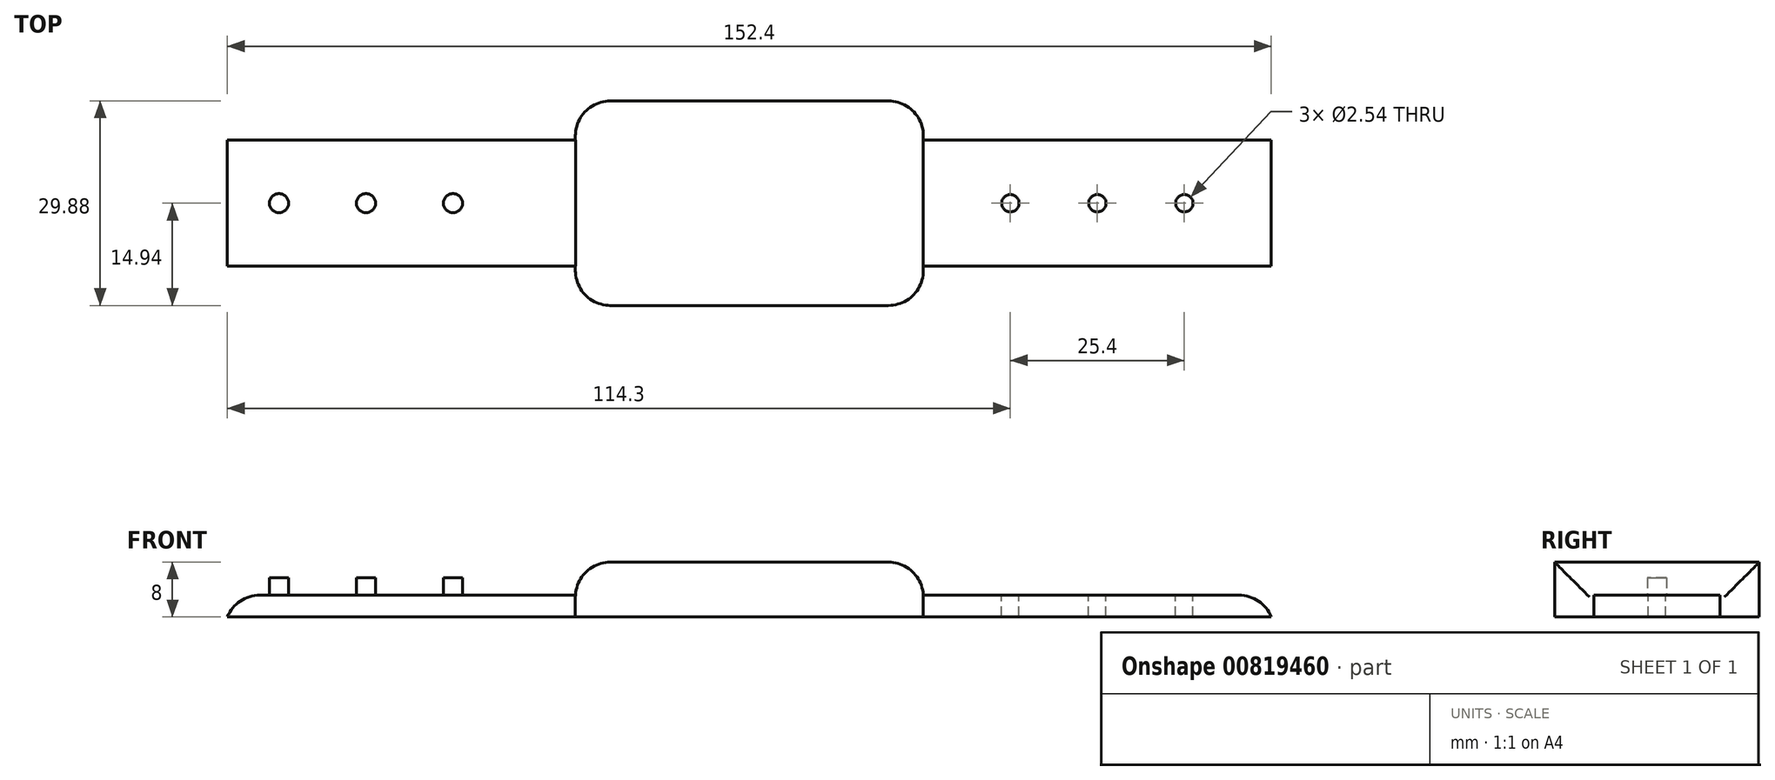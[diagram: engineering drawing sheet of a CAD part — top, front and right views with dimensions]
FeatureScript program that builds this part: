
annotation { "Feature Type Name" : "Feature", "Feature Type Description" : "" }
export const myFeature = defineFeature(function(context is Context, id is Id, definition is map)
    precondition{}
    {
        {
            var Q0;
            Q0=qCreatedBy(makeId("Top.planeOp"),FACE);
            var sketch = newSketch(context, id + "F0", { "sketchPlane" : qUnion([Q0])});
            skLineSegment(sketch, "E0.bottom", {"start": v(25.4, -14.94) * mm, "end": v(-25.4, -14.94) * mm});
            skLineSegment(sketch, "E0.top", {"start": v(25.4, 14.94) * mm, "end": v(-25.4, 14.94) * mm});
            skLineSegment(sketch, "E0.left", {"start": v(25.4, -14.94) * mm, "end": v(25.4, 14.94) * mm});
            skLineSegment(sketch, "E0.right", {"start": v(-25.4, -14.94) * mm, "end": v(-25.4, 14.94) * mm});
            skPoint(sketch, "E0.middle", {"position": v(0, 0) * mm});
            skLineSegment(sketch, "E1.bottom", {"start": v(-25.4, -9.2) * mm, "end": v(-76.2, -9.2) * mm});
            skLineSegment(sketch, "E1.top", {"start": v(-25.4, 9.2) * mm, "end": v(-76.2, 9.2) * mm});
            skLineSegment(sketch, "E1.left", {"start": v(-25.4, -9.2) * mm, "end": v(-25.4, 9.2) * mm});
            skLineSegment(sketch, "E1.right", {"start": v(-76.2, -9.2) * mm, "end": v(-76.2, 9.2) * mm});
            skLineSegment(sketch, "E2.MirrorCS", {"start": v(25.4, 9.2) * mm, "end": v(76.2, 9.2) * mm});
            skLineSegment(sketch, "E3.MirrorCS", {"start": v(76.2, -9.2) * mm, "end": v(76.2, 9.2) * mm});
            skLineSegment(sketch, "E4.MirrorCS", {"start": v(25.4, -9.2) * mm, "end": v(76.2, -9.2) * mm});
            skSolve(sketch);
        }
        {
            var Q0;
            Q0=qSketchRegion(id+"F0",true);
            extrude(context, id + "F1", {"entities" : qUnion([Q0]), "depth" : 3.17 * mm, "offsetDistance" : 25.4 * mm});
        }
        {
            var Q0;
            Q0=makeQuery(id+"F1.opExtrude","CAP_FACE",FACE,{"disambiguationData":[OSD([sQuery(id+"F0.wireOp",EDGE,"E0.bottom"),sQuery(id+"F0.wireOp",EDGE,"E0.top"),sQuery(id+"F0.wireOp",EDGE,"E0.left"),sQuery(id+"F0.wireOp",EDGE,"E0.right"),sQuery(id+"F0.wireOp",EDGE,"E1.bottom"),sQuery(id+"F0.wireOp",EDGE,"E1.top"),sQuery(id+"F0.wireOp",EDGE,"E1.right"),sQuery(id+"F0.wireOp",EDGE,"E2.MirrorCS"),sQuery(id+"F0.wireOp",EDGE,"E3.MirrorCS"),sQuery(id+"F0.wireOp",EDGE,"E4.MirrorCS")])],"isStart":false});
            var sketch = newSketch(context, id + "F2", { "sketchPlane" : qUnion([Q0])});
            skLineSegment(sketch, "E5", {"start": v(76.2, 0) * mm, "end": v(63.5, 0) * mm, "construction": true});
            skLineSegment(sketch, "E6", {"start": v(63.5, 0) * mm, "end": v(50.8, 0) * mm, "construction": true});
            skLineSegment(sketch, "E7", {"start": v(50.8, 0) * mm, "end": v(38.1, 0) * mm, "construction": true});
            skCircle(sketch, "E8", {"center": v(63.5, 0) * mm, "radius": 1.27 * mm});
            skCircle(sketch, "E9", {"center": v(50.8, 0) * mm, "radius": 1.27 * mm});
            skCircle(sketch, "E10", {"center": v(38.1, 0) * mm, "radius": 1.27 * mm});
            skSolve(sketch);
        }
        {
            var Q0;
            Q0=qSketchRegion(id+"F2",true);
            extrude(context, id + "F3", {"entities" : qUnion([Q0]), "operationType" : NewBodyOperationType.REMOVE, "oppositeDirection" : true, "depth" : 25.4 * mm, "offsetDistance" : 25.4 * mm});
        }
        {
            var Q0;
            Q0=makeQuery(id+"F2.imprint","IMPRINT",FACE,{"disambiguationData":[TD([[makeQuery(id+"F2.imprint","IMPRINT",EDGE,{"derivedFrom":sQuery(id+"F2.wireOp",EDGE,"E8")}),-1.0]])]});
            var sketch = newSketch(context, id + "F4", { "sketchPlane" : qUnion([Q0])});
            skLineSegment(sketch, "E11", {"start": v(-68.67, 0) * mm, "end": v(-55.97, 0) * mm, "construction": true});
            skLineSegment(sketch, "E12", {"start": v(-55.97, 0) * mm, "end": v(-43.27, 0) * mm, "construction": true});
            skCircle(sketch, "E13", {"center": v(-68.67, 0) * mm, "radius": 1.4 * mm});
            skCircle(sketch, "E14", {"center": v(-55.97, 0) * mm, "radius": 1.4 * mm});
            skCircle(sketch, "E15", {"center": v(-43.27, 0) * mm, "radius": 1.4 * mm});
            skSolve(sketch);
        }
        {
            var Q0;
            Q0=qSketchRegion(id+"F4",true);
            extrude(context, id + "F5", {"entities" : qUnion([Q0]), "operationType" : NewBodyOperationType.ADD, "depth" : 2.54 * mm, "offsetDistance" : 25.4 * mm});
        }
        {
            var Q0;
            Q0=makeQuery(id+"F1.opExtrude","CAP_FACE",FACE,{"disambiguationData":[OSD([sQuery(id+"F0.wireOp",EDGE,"E0.bottom"),sQuery(id+"F0.wireOp",EDGE,"E0.top"),sQuery(id+"F0.wireOp",EDGE,"E0.left"),sQuery(id+"F0.wireOp",EDGE,"E0.right"),sQuery(id+"F0.wireOp",EDGE,"E1.bottom"),sQuery(id+"F0.wireOp",EDGE,"E1.top"),sQuery(id+"F0.wireOp",EDGE,"E1.right"),sQuery(id+"F0.wireOp",EDGE,"E2.MirrorCS"),sQuery(id+"F0.wireOp",EDGE,"E3.MirrorCS"),sQuery(id+"F0.wireOp",EDGE,"E4.MirrorCS")])],"isStart":false});
            var sketch = newSketch(context, id + "F6", { "sketchPlane" : qUnion([Q0])});
            skLineSegment(sketch, "E16.bottom", {"start": v(-25.4, 14.94) * mm, "end": v(25.4, 14.94) * mm});
            skLineSegment(sketch, "E16.top", {"start": v(-25.4, -14.94) * mm, "end": v(25.4, -14.94) * mm});
            skLineSegment(sketch, "E16.left", {"start": v(-25.4, 14.94) * mm, "end": v(-25.4, -14.94) * mm});
            skLineSegment(sketch, "E16.right", {"start": v(25.4, 14.94) * mm, "end": v(25.4, -14.94) * mm});
            skSolve(sketch);
        }
        {
            var Q0;
            Q0=qSketchRegion(id+"F6",true);
            extrude(context, id + "F7", {"entities" : qUnion([Q0]), "operationType" : NewBodyOperationType.ADD, "depth" : 4.83 * mm, "offsetDistance" : 25.4 * mm});
        }
        {
            var Q0;
            Q0=makeQuery(id+"F7.opExtrude","CAP_EDGE",EDGE,{"disambiguationData":[OSD([sQuery(id+"F6.wireOp",EDGE,"E16.right")])],"isStart":false});
            var Q1;
            Q1=makeQuery(id+"F7.opExtrude","CAP_EDGE",EDGE,{"disambiguationData":[OSD([sQuery(id+"F6.wireOp",EDGE,"E16.left")])],"isStart":false});
            var Q2;
            Q2=makeQuery(id+"F7.boolean.opBoolean","MERGE",EDGE,{"derivedFrom":[makeQuery(id+"F1.opExtrude","SWEPT_EDGE",EDGE,{"disambiguationData":[OSD([sQuery(id+"F0.wireOp",EDGE,"E0.top"),sQuery(id+"F0.wireOp",EDGE,"E0.right")])]}),makeQuery(id+"F7.opExtrude","SWEPT_EDGE",EDGE,{"disambiguationData":[OSD([sQuery(id+"F6.wireOp",EDGE,"E16.bottom"),sQuery(id+"F6.wireOp",EDGE,"E16.left")])]})]});
            var Q3;
            Q3=makeQuery(id+"F7.boolean.opBoolean","MERGE",EDGE,{"derivedFrom":[makeQuery(id+"F1.opExtrude","SWEPT_EDGE",EDGE,{"disambiguationData":[OSD([sQuery(id+"F0.wireOp",EDGE,"E0.bottom"),sQuery(id+"F0.wireOp",EDGE,"E0.right")])]}),makeQuery(id+"F7.opExtrude","SWEPT_EDGE",EDGE,{"disambiguationData":[OSD([sQuery(id+"F6.wireOp",EDGE,"E16.top"),sQuery(id+"F6.wireOp",EDGE,"E16.left")])]})]});
            var Q4;
            Q4=makeQuery(id+"F7.boolean.opBoolean","MERGE",EDGE,{"derivedFrom":[makeQuery(id+"F1.opExtrude","SWEPT_EDGE",EDGE,{"disambiguationData":[OSD([sQuery(id+"F0.wireOp",EDGE,"E0.bottom"),sQuery(id+"F0.wireOp",EDGE,"E0.left")])]}),makeQuery(id+"F7.opExtrude","SWEPT_EDGE",EDGE,{"disambiguationData":[OSD([sQuery(id+"F6.wireOp",EDGE,"E16.top"),sQuery(id+"F6.wireOp",EDGE,"E16.right")])]})]});
            var Q5;
            Q5=makeQuery(id+"F7.boolean.opBoolean","MERGE",EDGE,{"derivedFrom":[makeQuery(id+"F1.opExtrude","SWEPT_EDGE",EDGE,{"disambiguationData":[OSD([sQuery(id+"F0.wireOp",EDGE,"E0.top"),sQuery(id+"F0.wireOp",EDGE,"E0.left")])]}),makeQuery(id+"F7.opExtrude","SWEPT_EDGE",EDGE,{"disambiguationData":[OSD([sQuery(id+"F6.wireOp",EDGE,"E16.bottom"),sQuery(id+"F6.wireOp",EDGE,"E16.right")])]})]});
            fillet(context, id + "F8", {"entities" : qUnion([Q0, Q1, Q2, Q3, Q4, Q5]), "radius" : 5.08 * mm, "tangentPropagation" : true, "allowEdgeOverflow" : false});
        }
        {
            var Q0;
            Q0=makeQuery(id+"F1.opExtrude","CAP_EDGE",EDGE,{"disambiguationData":[OSD([sQuery(id+"F0.wireOp",EDGE,"E3.MirrorCS")])],"isStart":false});
            var Q1;
            Q1=makeQuery(id+"F1.opExtrude","CAP_EDGE",EDGE,{"disambiguationData":[OSD([sQuery(id+"F0.wireOp",EDGE,"E1.right")])],"isStart":false});
            fillet(context, id + "F9", {"entities" : qUnion([Q0, Q1]), "radius" : 5.08 * mm, "tangentPropagation" : true, "allowEdgeOverflow" : false});
        }
    });
